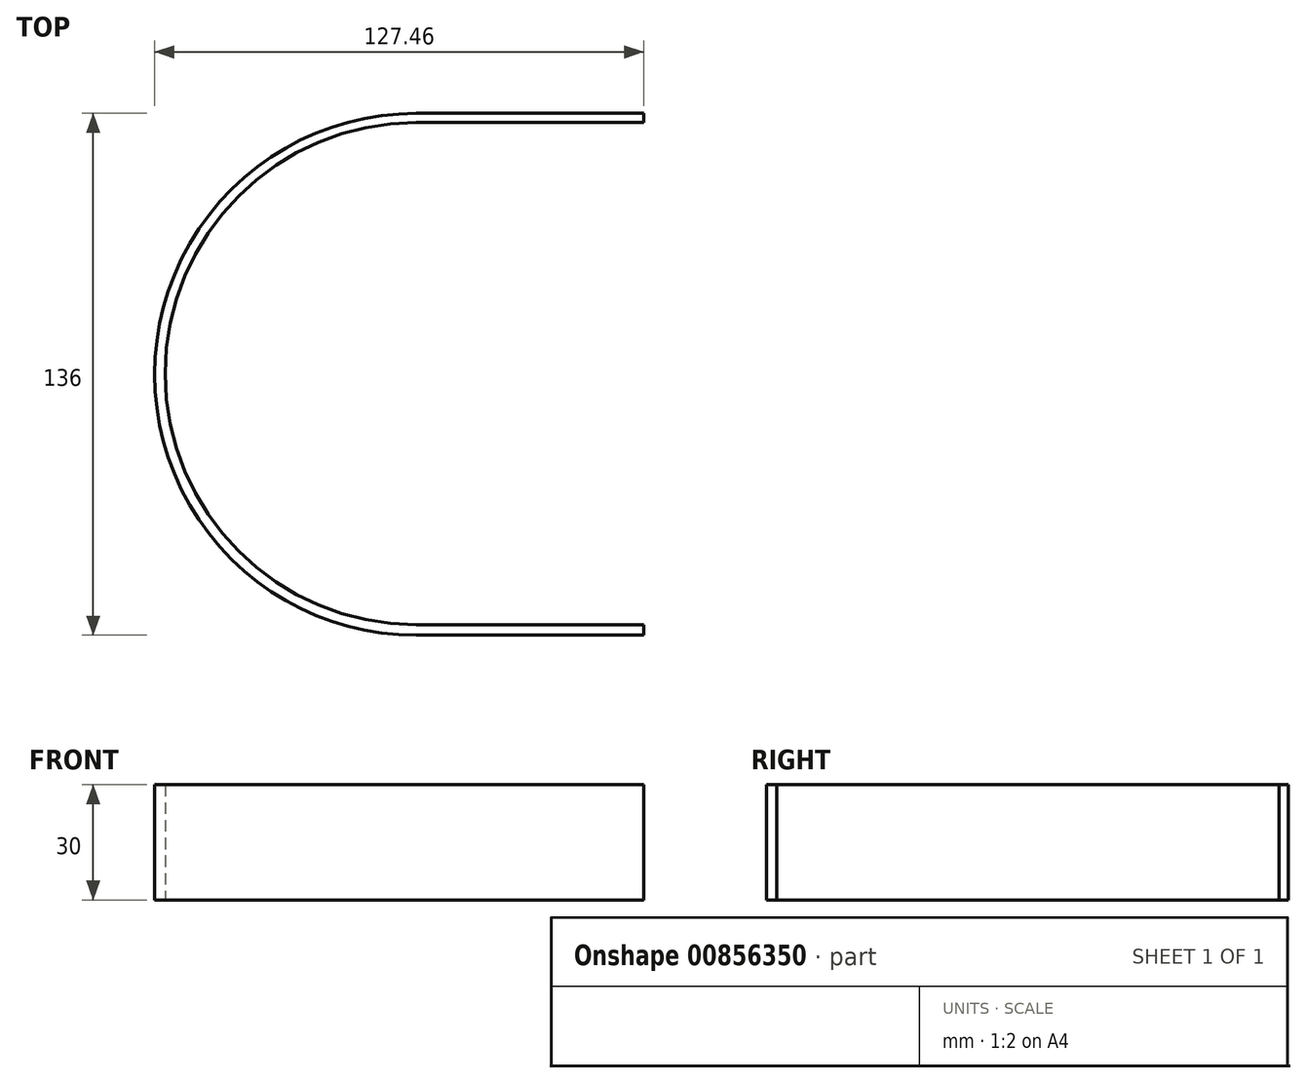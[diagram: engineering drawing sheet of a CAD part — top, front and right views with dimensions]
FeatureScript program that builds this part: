
annotation { "Feature Type Name" : "Feature", "Feature Type Description" : "" }
export const myFeature = defineFeature(function(context is Context, id is Id, definition is map)
    precondition{}
    {
        {
            var Q0;
            Q0=qCreatedBy(makeId("Top.planeOp"),FACE);
            var sketch = newSketch(context, id + "F0", { "sketchPlane" : qUnion([Q0])});
            skLineSegment(sketch, "E0", {"start": v(40.27, 67.9) * mm, "end": v(-19, 67.9) * mm});
            skLineSegment(sketch, "E1", {"start": v(40.27, -68.1) * mm, "end": v(-19, -68.1) * mm});
            skArc(sketch, "E2", {"start": v(-19, 67.9) * mm, "mid": v(-87.2, -0.1) * mm, "end": v(-19, -68.1) * mm});
            skLineSegment(sketch, "E3", {"start": v(40.27, 67.9) * mm, "end": v(40.27, 65.55) * mm});
            skLineSegment(sketch, "E4", {"start": v(40.27, 65.55) * mm, "end": v(-19, 65.55) * mm});
            skLineSegment(sketch, "E5", {"start": v(40.27, -68.1) * mm, "end": v(40.27, -65.36) * mm});
            skLineSegment(sketch, "E6", {"start": v(40.27, -65.36) * mm, "end": v(-19, -65.36) * mm});
            skArc(sketch, "E7", {"start": v(-19, 65.55) * mm, "mid": v(-84.46, 0.1) * mm, "end": v(-19, -65.36) * mm});
            skSolve(sketch);
        }
        {
            var Q0;
            Q0=makeQuery(id+"F0.imprint","IMPRINT",FACE,{"disambiguationData":[TD([[makeQuery(id+"F0.imprint","IMPRINT",EDGE,{"derivedFrom":sQuery(id+"F0.wireOp",EDGE,"E0")}),1.0]])]});
            extrude(context, id + "F1", {"entities" : qUnion([Q0]), "depth" : 30 * mm, "offsetDistance" : 25 * mm});
        }
    });
